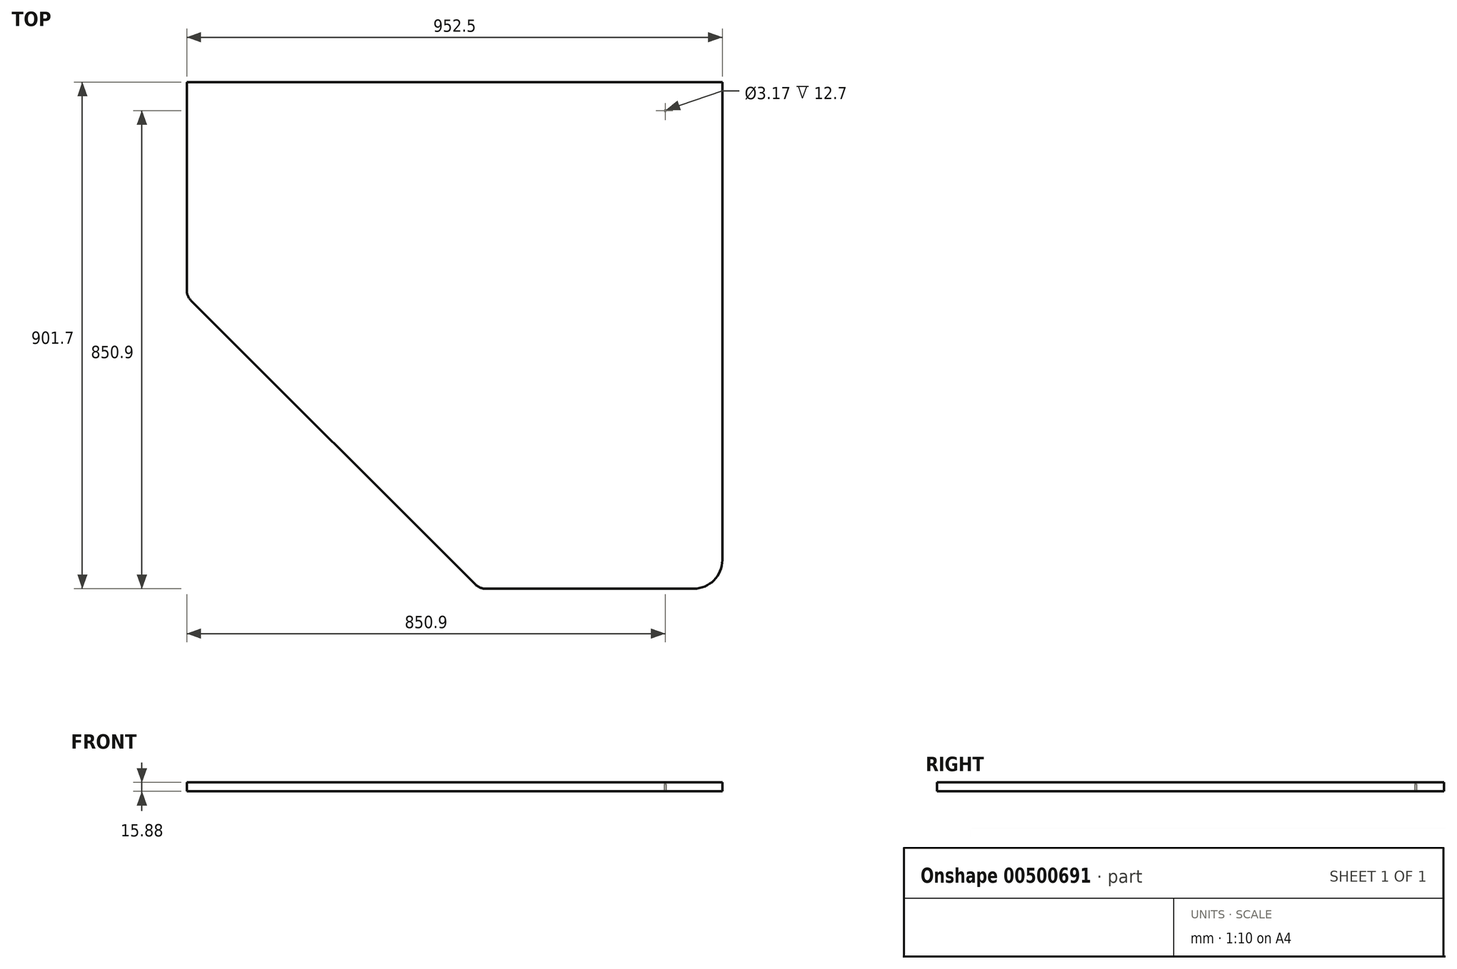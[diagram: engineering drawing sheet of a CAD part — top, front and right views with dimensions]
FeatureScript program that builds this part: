
annotation { "Feature Type Name" : "Feature", "Feature Type Description" : "" }
export const myFeature = defineFeature(function(context is Context, id is Id, definition is map)
    precondition{}
    {
        {
            var Q0;
            Q0=qCreatedBy(makeId("Top.planeOp"),FACE);
            var sketch = newSketch(context, id + "F0", { "sketchPlane" : qUnion([Q0])});
            skLineSegment(sketch, "E0", {"start": v(0, 0) * mm, "end": v(-952.5, 0) * mm});
            skLineSegment(sketch, "E1", {"start": v(-952.5, 0) * mm, "end": v(-952.5, -381) * mm});
            skLineSegment(sketch, "E2", {"start": v(-952.5, -381) * mm, "end": v(-431.8, -901.7) * mm});
            skLineSegment(sketch, "E3", {"start": v(-431.8, -901.7) * mm, "end": v(0, -901.7) * mm});
            skLineSegment(sketch, "E4", {"start": v(0, -901.7) * mm, "end": v(0, 0) * mm});
            skSolve(sketch);
        }
        {
            var Q0;
            Q0=makeQuery(id+"F0.imprint","IMPRINT",FACE,{"disambiguationData":[TD([[makeQuery(id+"F0.imprint","IMPRINT",EDGE,{"derivedFrom":sQuery(id+"F0.wireOp",EDGE,"E0")}),1.0]])]});
            extrude(context, id + "F1", {"entities" : qUnion([Q0]), "oppositeDirection" : true, "depth" : 15.88 * mm, "offsetDistance" : 25.4 * mm});
        }
        {
            var Q0;
            Q0=makeQuery(id+"F1.opExtrude","SWEPT_EDGE",EDGE,{"disambiguationData":[OSD([sQuery(id+"F0.wireOp",EDGE,"E3"),sQuery(id+"F0.wireOp",EDGE,"E4")])]});
            fillet(context, id + "F2", {"entities" : qUnion([Q0]), "radius" : 50.8 * mm, "tangentPropagation" : true, "allowEdgeOverflow" : false});
        }
        {
            var Q0;
            Q0=makeQuery(id+"F1.opExtrude","SWEPT_EDGE",EDGE,{"disambiguationData":[OSD([sQuery(id+"F0.wireOp",EDGE,"E2"),sQuery(id+"F0.wireOp",EDGE,"E3")])]});
            fillet(context, id + "F3", {"entities" : qUnion([Q0]), "radius" : 25.4 * mm, "tangentPropagation" : true, "allowEdgeOverflow" : false});
        }
        {
            var Q0;
            Q0=makeQuery(id+"F1.opExtrude","SWEPT_EDGE",EDGE,{"disambiguationData":[OSD([sQuery(id+"F0.wireOp",EDGE,"E1"),sQuery(id+"F0.wireOp",EDGE,"E2")])]});
            fillet(context, id + "F4", {"entities" : qUnion([Q0]), "radius" : 25.4 * mm, "tangentPropagation" : true, "allowEdgeOverflow" : false});
        }
        {
            var Q0;
            Q0=makeQuery(id+"F1.opExtrude","CAP_FACE",FACE,{"disambiguationData":[OSD([sQuery(id+"F0.wireOp",EDGE,"E0"),sQuery(id+"F0.wireOp",EDGE,"E1"),sQuery(id+"F0.wireOp",EDGE,"E2"),sQuery(id+"F0.wireOp",EDGE,"E3"),sQuery(id+"F0.wireOp",EDGE,"E4")])],"isStart":false});
            var sketch = newSketch(context, id + "F5", { "sketchPlane" : qUnion([Q0])});
            skPoint(sketch, "E5", {"position": v(-101.6, 50.8) * mm});
            skCircle(sketch, "E6", {"center": v(-101.6, 50.8) * mm, "radius": 1.59 * mm});
            skSolve(sketch);
        }
        {
            var Q0;
            Q0 = qSketchRegion(id + "F5", true);
            extrude(context, id + "F6", {"entities" : qUnion([Q0]), "operationType" : NewBodyOperationType.REMOVE, "oppositeDirection" : true, "depth" : 12.7 * mm, "offsetDistance" : 25.4 * mm});
        }
    });
